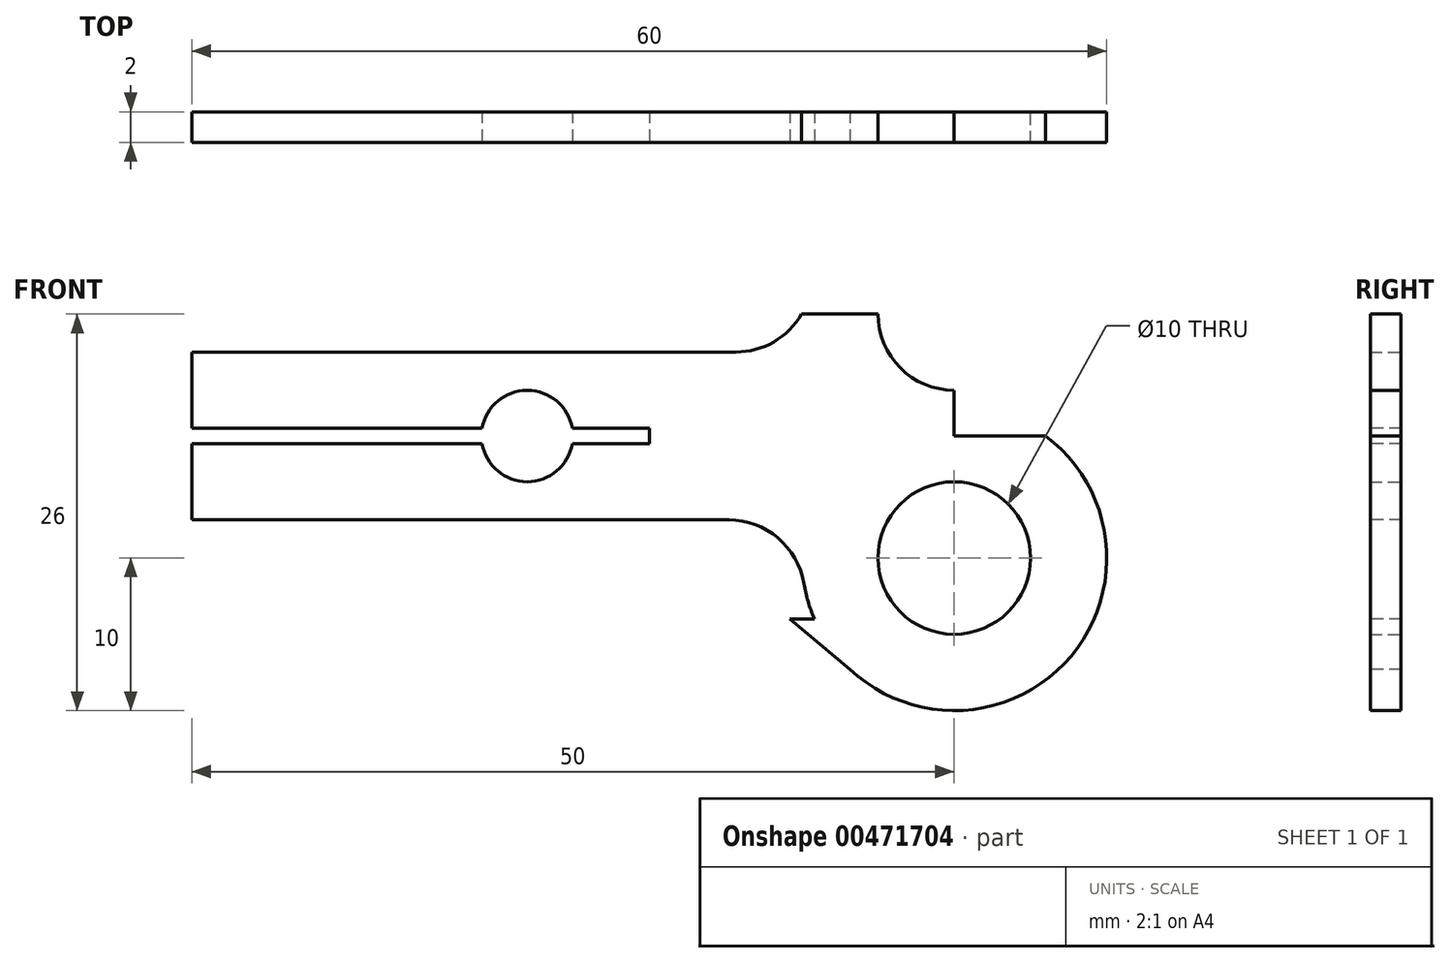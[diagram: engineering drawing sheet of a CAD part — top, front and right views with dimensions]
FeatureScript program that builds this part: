
annotation { "Feature Type Name" : "Feature", "Feature Type Description" : "" }
export const myFeature = defineFeature(function(context is Context, id is Id, definition is map)
    precondition{}
    {
        {
            var Q0;
            Q0=qCreatedBy(makeId("Front.planeOp"),FACE);
            var sketch = newSketch(context, id + "F0", { "sketchPlane" : qUnion([Q0])});
            skLineSegment(sketch, "E0.bottom", {"start": v(0, 0) * mm, "end": v(40, 0) * mm});
            skLineSegment(sketch, "E0.top", {"start": v(0, 11) * mm, "end": v(40, 11) * mm});
            skLineSegment(sketch, "E0.left", {"start": v(0, 0) * mm, "end": v(0, 11) * mm});
            skLineSegment(sketch, "E0.right", {"start": v(40, 0) * mm, "end": v(40, 11) * mm});
            skCircle(sketch, "E1", {"center": v(50, -2.5) * mm, "radius": 10 * mm});
            skCircle(sketch, "E2", {"center": v(50, 13.5) * mm, "radius": 10 * mm});
            skCircle(sketch, "E3", {"center": v(50, -2.5) * mm, "radius": 5 * mm});
            skCircle(sketch, "E4", {"center": v(50, 13.5) * mm, "radius": 5 * mm});
            skCircle(sketch, "E5", {"center": v(22, 5.5) * mm, "radius": 3 * mm});
            skPoint(sketch, "E5.centerSnap0", {"position": v(0, 5.5) * mm});
            skLineSegment(sketch, "E6", {"start": v(0, 5.5) * mm, "end": v(70.53, 5.5) * mm});
            skLineSegment(sketch, "E7.bottom", {"start": v(40, -2.5) * mm, "end": v(50, -2.5) * mm});
            skLineSegment(sketch, "E7.top", {"start": v(40, 13.5) * mm, "end": v(50, 13.5) * mm});
            skLineSegment(sketch, "E7.left", {"start": v(40, -2.5) * mm, "end": v(40, 13.5) * mm});
            skLineSegment(sketch, "E7.right", {"start": v(50, -2.5) * mm, "end": v(50, 13.5) * mm});
            skSolve(sketch);
        }
        {
            var Q0;
            Q0=makeQuery(id+"F0.imprint","IMPRINT",FACE,{"disambiguationData":[TD([[makeQuery(id+"F0.imprint","IMPRINT",EDGE,{"derivedFrom":sQuery(id+"F0.wireOp",EDGE,"E0.bottom")}),1.0]])]});
            var Q1;
            {var subQ0=sQuery(id+"F0.wireOp",EDGE,"E0.right");Q1=makeQuery(id+"F0.imprint","IMPRINT",FACE,{"disambiguationData":[TD([[makeQuery(id+"F0.imprint","IMPRINT",EDGE,{"derivedFrom":subQ0}),-1.0]])]});}
            var Q2;
            {var subQ0=sQuery(id+"F0.wireOp",EDGE,"E2");var subQ2=sQuery(id+"F0.wireOp",EDGE,"E1");var subQ3=makeQuery(id+"F0.imprint","INTERSECT",VERTEX,{"disambiguationData":[OD(0.0)],"derivedFrom":[subQ2,subQ0]});Q2=makeQuery(id+"F0.imprint","IMPRINT",FACE,{"disambiguationData":[TD([[makeQuery(id+"F0.imprint","IMPRINT",EDGE,{"disambiguationData":[TD([[subQ3,-1.0]])],"derivedFrom":subQ2}),-1.0]])]});}
            var Q3;
            {var subQ0=sQuery(id+"F0.wireOp",EDGE,"E2");var subQ1=sQuery(id+"F0.wireOp",EDGE,"E1");var subQ2=makeQuery(id+"F0.imprint","INTERSECT",VERTEX,{"disambiguationData":[OD(0.0)],"derivedFrom":[subQ1,subQ0]});Q3=makeQuery(id+"F0.imprint","IMPRINT",FACE,{"disambiguationData":[TD([[makeQuery(id+"F0.imprint","IMPRINT",EDGE,{"disambiguationData":[TD([[subQ2,-1.0]])],"derivedFrom":subQ1}),1.0]])]});}
            var Q4;
            {var subQ0=sQuery(id+"F0.wireOp",EDGE,"E2");var subQ1=sQuery(id+"F0.wireOp",EDGE,"E1");var subQ2=makeQuery(id+"F0.imprint","INTERSECT",VERTEX,{"disambiguationData":[OD(1.0)],"derivedFrom":[subQ1,subQ0]});Q4=makeQuery(id+"F0.imprint","IMPRINT",FACE,{"disambiguationData":[TD([[makeQuery(id+"F0.imprint","IMPRINT",EDGE,{"disambiguationData":[TD([[subQ2,-1.0]])],"derivedFrom":subQ0}),-1.0]])]});}
            var Q5;
            {var subQ5=sQuery(id+"F0.wireOp",EDGE,"E0.top");Q5=makeQuery(id+"F0.imprint","IMPRINT",FACE,{"disambiguationData":[TD([[makeQuery(id+"F0.imprint","IMPRINT",EDGE,{"derivedFrom":subQ5}),-1.0]])]});}
            var Q6;
            {var subQ0=sQuery(id+"F0.wireOp",EDGE,"E3");var subQ1=sQuery(id+"F0.wireOp",EDGE,"E2");var subQ2=makeQuery(id+"F0.imprint","INTERSECT",VERTEX,{"disambiguationData":[OD(0.0)],"derivedFrom":[subQ1,subQ0]});Q6=makeQuery(id+"F0.imprint","IMPRINT",FACE,{"disambiguationData":[TD([[makeQuery(id+"F0.imprint","IMPRINT",EDGE,{"disambiguationData":[TD([[subQ2,1.0]])],"derivedFrom":subQ0}),-1.0]])]});}
            var Q7;
            {var subQ0=sQuery(id+"F0.wireOp",EDGE,"E7.left");var subQ1=sQuery(id+"F0.wireOp",EDGE,"E7.top");var subQ2=makeQuery(id+"F0.imprint","INTERSECT",VERTEX,{"derivedFrom":[subQ1,subQ0]});Q7=makeQuery(id+"F0.imprint","IMPRINT",FACE,{"disambiguationData":[TD([[makeQuery(id+"F0.imprint","IMPRINT",EDGE,{"disambiguationData":[TD([[subQ2,-1.0]])],"derivedFrom":subQ1}),-1.0]])]});}
            var Q8;
            {var subQ0=sQuery(id+"F0.wireOp",EDGE,"E7.right");var subQ3=sQuery(id+"F0.wireOp",EDGE,"E6");var subQ5=makeQuery(id+"F0.imprint","INTERSECT",VERTEX,{"derivedFrom":[subQ3,subQ0]});Q8=makeQuery(id+"F0.imprint","IMPRINT",FACE,{"disambiguationData":[TD([[makeQuery(id+"F0.imprint","IMPRINT",EDGE,{"disambiguationData":[TD([[subQ5,1.0]])],"derivedFrom":subQ3}),1.0]])]});}
            var Q9;
            {var subQ0=sQuery(id+"F0.wireOp",EDGE,"E6");var subQ3=sQuery(id+"F0.wireOp",EDGE,"E7.right");var subQ5=makeQuery(id+"F0.imprint","INTERSECT",VERTEX,{"derivedFrom":[subQ0,subQ3]});Q9=makeQuery(id+"F0.imprint","IMPRINT",FACE,{"disambiguationData":[TD([[makeQuery(id+"F0.imprint","IMPRINT",EDGE,{"disambiguationData":[TD([[subQ5,1.0]])],"derivedFrom":subQ0}),-1.0]])]});}
            var Q10;
            {var subQ0=sQuery(id+"F0.wireOp",EDGE,"E7.left");var subQ1=sQuery(id+"F0.wireOp",EDGE,"E2");var subQ2=makeQuery(id+"F0.imprint","INTERSECT",VERTEX,{"derivedFrom":[subQ1,subQ0]});Q10=makeQuery(id+"F0.imprint","IMPRINT",FACE,{"disambiguationData":[TD([[makeQuery(id+"F0.imprint","IMPRINT",EDGE,{"disambiguationData":[TD([[subQ2,1.0]])],"derivedFrom":subQ0}),-1.0]])]});}
            var Q11;
            {var subQ1=sQuery(id+"F0.wireOp",EDGE,"E0.top");var subQ6=sQuery(id+"F0.wireOp",EDGE,"E0.left");var subQ11=makeQuery(id+"F0.imprint","INTERSECT",VERTEX,{"derivedFrom":[subQ1,subQ6]});Q11=makeQuery(id+"F0.imprint","IMPRINT",FACE,{"disambiguationData":[TD([[makeQuery(id+"F0.imprint","IMPRINT",EDGE,{"disambiguationData":[TD([[subQ11,-1.0]])],"derivedFrom":subQ1}),-1.0]])]});}
            var Q12;
            {var subQ5=sQuery(id+"F0.wireOp",EDGE,"E0.bottom");var subQ9=sQuery(id+"F0.wireOp",EDGE,"E0.left");var subQ10=makeQuery(id+"F0.imprint","INTERSECT",VERTEX,{"derivedFrom":[subQ5,subQ9]});Q12=makeQuery(id+"F0.imprint","IMPRINT",FACE,{"disambiguationData":[TD([[makeQuery(id+"F0.imprint","IMPRINT",EDGE,{"disambiguationData":[TD([[subQ10,-1.0]])],"derivedFrom":subQ5}),1.0]])]});}
            var Q13;
            {var subQ0=sQuery(id+"F0.wireOp",EDGE,"E6");var subQ3=sQuery(id+"F0.wireOp",EDGE,"E7.right");var subQ5=makeQuery(id+"F0.imprint","INTERSECT",VERTEX,{"derivedFrom":[subQ0,subQ3]});Q13=makeQuery(id+"F0.imprint","IMPRINT",FACE,{"disambiguationData":[TD([[makeQuery(id+"F0.imprint","IMPRINT",EDGE,{"disambiguationData":[TD([[subQ5,-1.0]])],"derivedFrom":subQ0}),-1.0]])]});}
            var Q14;
            {var subQ0=sQuery(id+"F0.wireOp",EDGE,"E7.left");var subQ1=sQuery(id+"F0.wireOp",EDGE,"E1");var subQ2=makeQuery(id+"F0.imprint","INTERSECT",VERTEX,{"derivedFrom":[subQ1,subQ0]});Q14=makeQuery(id+"F0.imprint","IMPRINT",FACE,{"disambiguationData":[TD([[makeQuery(id+"F0.imprint","IMPRINT",EDGE,{"disambiguationData":[TD([[subQ2,-1.0]])],"derivedFrom":subQ0}),-1.0]])]});}
            extrude(context, id + "F1", {"entities" : qUnion([Q0, Q1, Q2, Q3, Q4, Q5, Q6, Q7, Q8, Q9, Q10, Q11, Q12, Q13, Q14]), "depth" : 2 * mm, "offsetDistance" : 25 * mm});
        }
        {
            var Q0;
            Q0=makeQuery(id+"F1.opExtrude","SWEPT_EDGE",EDGE,{"disambiguationData":[OSD([sQuery(id+"F0.wireOp",EDGE,"E0.top"),sQuery(id+"F0.wireOp",EDGE,"E0.right"),sQuery(id+"F0.wireOp",EDGE,"E2")])]});
            var Q1;
            Q1=makeQuery(id+"F1.opExtrude","SWEPT_EDGE",EDGE,{"disambiguationData":[OSD([sQuery(id+"F0.wireOp",EDGE,"E0.bottom"),sQuery(id+"F0.wireOp",EDGE,"E0.right"),sQuery(id+"F0.wireOp",EDGE,"E1")])]});
            fillet(context, id + "F2", {"entities" : qUnion([Q0, Q1]), "radius" : 5 * mm, "tangentPropagation" : true, "allowEdgeOverflow" : false});
        }
        {
            var Q0;
            Q0=makeQuery(id+"F1.opExtrude","CAP_FACE",FACE,{"disambiguationData":[OSD([sQuery(id+"F0.wireOp",EDGE,"E0.bottom"),sQuery(id+"F0.wireOp",EDGE,"E0.top"),sQuery(id+"F0.wireOp",EDGE,"E0.left"),sQuery(id+"F0.wireOp",EDGE,"E1"),sQuery(id+"F0.wireOp",EDGE,"E2"),sQuery(id+"F0.wireOp",EDGE,"E3"),sQuery(id+"F0.wireOp",EDGE,"E4"),sQuery(id+"F0.wireOp",EDGE,"E5"),sQuery(id+"F0.wireOp",EDGE,"E7.left")])],"isStart":false});
            var sketch = newSketch(context, id + "F3", { "sketchPlane" : qUnion([Q0])});
            skLineSegment(sketch, "E8.bottom", {"start": v(0, 6) * mm, "end": v(30, 6) * mm});
            skLineSegment(sketch, "E9", {"start": v(0, 6) * mm, "end": v(0, 5) * mm});
            skLineSegment(sketch, "E10", {"start": v(0, 5) * mm, "end": v(30, 5) * mm});
            skLineSegment(sketch, "E11", {"start": v(30, 6) * mm, "end": v(30, 5) * mm});
            skSolve(sketch);
        }
        {
            var Q0;
            {var subQ0=sQuery(id+"F3.wireOp",EDGE,"E8.left");Q0=makeQuery(id+"F3.imprint","IMPRINT",FACE,{"disambiguationData":[TD([[makeQuery(id+"F3.imprint","IMPRINT",EDGE,{"derivedFrom":subQ0}),-1.0]])]});}
            var Q1;
            {var subQ0=sQuery(id+"F3.wireOp",EDGE,"E8.right");Q1=makeQuery(id+"F3.imprint","IMPRINT",FACE,{"disambiguationData":[TD([[makeQuery(id+"F3.imprint","IMPRINT",EDGE,{"derivedFrom":subQ0}),-1.0]])]});}
            var Q2;
            {var subQ0=sQuery(id+"F3.wireOp",EDGE,"E9");Q2=makeQuery(id+"F3.imprint","IMPRINT",FACE,{"disambiguationData":[TD([[makeQuery(id+"F3.imprint","IMPRINT",EDGE,{"derivedFrom":subQ0}),-1.0]])]});}
            var Q3;
            {var subQ0=sQuery(id+"F3.wireOp",EDGE,"E11");Q3=makeQuery(id+"F3.imprint","IMPRINT",FACE,{"disambiguationData":[TD([[makeQuery(id+"F3.imprint","IMPRINT",EDGE,{"derivedFrom":subQ0}),-1.0]])]});}
            extrude(context, id + "F4", {"entities" : qUnion([Q0, Q1, Q2, Q3]), "operationType" : NewBodyOperationType.REMOVE, "endBound" : BoundingType.UP_TO_NEXT, "oppositeDirection" : true, "depth" : 25 * mm});
        }
        {
            var Q0;
            Q0=makeQuery(id+"F1.opExtrude","CAP_FACE",FACE,{"disambiguationData":[OSD([sQuery(id+"F0.wireOp",EDGE,"E0.bottom"),sQuery(id+"F0.wireOp",EDGE,"E0.top"),sQuery(id+"F0.wireOp",EDGE,"E0.left"),sQuery(id+"F0.wireOp",EDGE,"E1"),sQuery(id+"F0.wireOp",EDGE,"E2"),sQuery(id+"F0.wireOp",EDGE,"E3"),sQuery(id+"F0.wireOp",EDGE,"E4"),sQuery(id+"F0.wireOp",EDGE,"E5"),sQuery(id+"F0.wireOp",EDGE,"E7.left")])],"isStart":false});
            var sketch = newSketch(context, id + "F5", { "sketchPlane" : qUnion([Q0])});
            skLineSegment(sketch, "E12", {"start": v(40.83, -6.5) * mm, "end": v(39.23, -6.5) * mm});
            skCircle(sketch, "E13", {"center": v(50, -2.5) * mm, "radius": 10 * mm});
            skLineSegment(sketch, "E14", {"start": v(39.23, -6.5) * mm, "end": v(44, -10.5) * mm});
            skSolve(sketch);
        }
        {
            var Q0;
            {var subQ0=sQuery(id+"F5.wireOp",EDGE,"E12");Q0=makeQuery(id+"F5.imprint","IMPRINT",FACE,{"disambiguationData":[TD([[makeQuery(id+"F5.imprint","IMPRINT",EDGE,{"derivedFrom":subQ0}),1.0]])]});}
            extrude(context, id + "F6", {"entities" : qUnion([Q0]), "operationType" : NewBodyOperationType.ADD, "oppositeDirection" : true, "depth" : 2 * mm, "offsetDistance" : 25 * mm});
        }
    });
